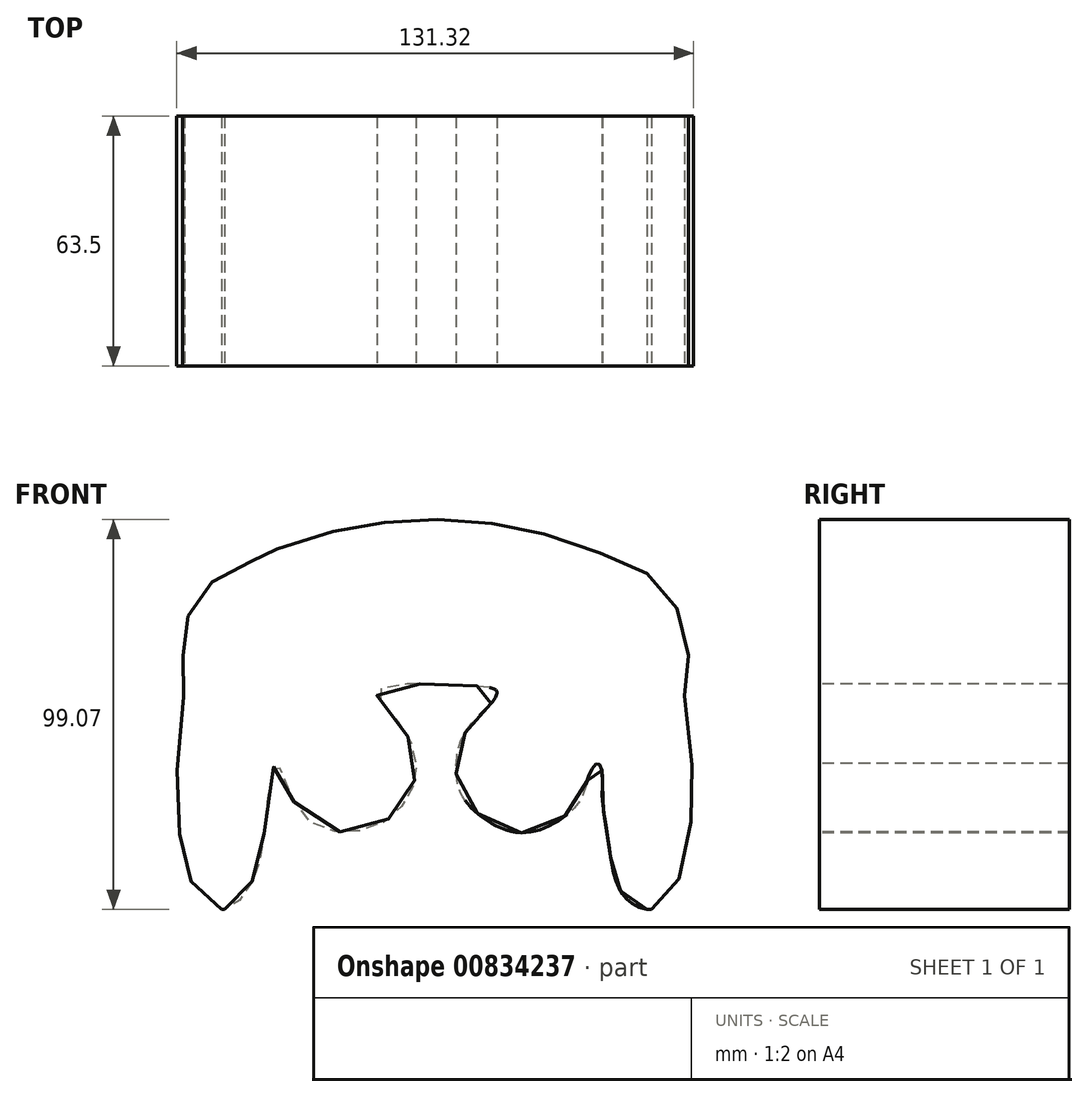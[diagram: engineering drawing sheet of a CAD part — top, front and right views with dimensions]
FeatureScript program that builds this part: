
annotation { "Feature Type Name" : "Feature", "Feature Type Description" : "" }
export const myFeature = defineFeature(function(context is Context, id is Id, definition is map)
    precondition{}
    {
        {
            var Q0;
            Q0=qCreatedBy(makeId("Front.planeOp"),FACE);
            var sketch = newSketch(context, id + "F0", { "sketchPlane" : qUnion([Q0])});
            skLineSegment(sketch, "E0.bottom", {"start": v(69.85, 50.8) * mm, "end": v(-69.85, 50.8) * mm});
            skLineSegment(sketch, "E0.top", {"start": v(69.85, -50.8) * mm, "end": v(-69.85, -50.8) * mm});
            skLineSegment(sketch, "E0.left", {"start": v(69.85, 50.8) * mm, "end": v(69.85, -50.8) * mm});
            skLineSegment(sketch, "E0.right", {"start": v(-69.85, 50.8) * mm, "end": v(-69.85, -50.8) * mm});
            skPoint(sketch, "E0.middle", {"position": v(0, 0) * mm});
            skSolve(sketch);
        }
        {
            var Q0;
            Q0=makeQuery(id+"F0.imprint","IMPRINT",FACE,{"disambiguationData":[TD([[makeQuery(id+"F0.imprint","IMPRINT",EDGE,{"derivedFrom":sQuery(id+"F0.wireOp",EDGE,"E0.bottom")}),1.0]])]});
            extrude(context, id + "F1", {"entities" : qUnion([Q0]), "depth" : 63.5 * mm, "offsetDistance" : 25.4 * mm});
        }
        {
            var Q0;
            Q0=makeQuery(id+"F1.opExtrude","CAP_FACE",FACE,{"disambiguationData":[OSD([sQuery(id+"F0.wireOp",EDGE,"E0.bottom"),sQuery(id+"F0.wireOp",EDGE,"E0.top"),sQuery(id+"F0.wireOp",EDGE,"E0.left"),sQuery(id+"F0.wireOp",EDGE,"E0.right")])],"isStart":false});
            var sketch = newSketch(context, id + "F2", { "sketchPlane" : qUnion([Q0])});
            skFitSpline(sketch, "E1", {"points": [v(0, 48.27) * mm, v(15.03, 47.3) * mm, v(29.07, 44.36) * mm, v(45.67, 38.5) * mm, v(56.3, 33.2) * mm, v(62.75, 23.96) * mm, v(64.87, 12.78) * mm, v(63.88, 5.12) * mm, v(66.07, -17.6) * mm, v(64.79, -32.74) * mm, v(60.06, -47.98) * mm, v(54.26, -50.8) * mm, v(49.52, -48.46) * mm, v(47.25, -45.36) * mm, v(45.47, -39.82) * mm, v(44.57, -33.56) * mm, v(42.96, -22.83) * mm, v(42.96, -16.21) * mm, v(41.89, -13.7) * mm, v(39.74, -16.27) * mm, v(37.49, -22.82) * mm, v(30.34, -29.13) * mm, v(21.4, -31.24) * mm, v(11.84, -26.94) * mm, v(6.48, -19.79) * mm, v(6.3, -10.3) * mm, v(8.8, -4.76) * mm, v(13.27, 0) * mm, v(16.18, 4.6) * mm, v(10.6, 5.97) * mm, v(-3.9, 6.5) * mm, v(-14.27, 4.36) * mm, v(-8.93, -3.18) * mm, v(-4.45, -12.75) * mm, v(-5.62, -20.77) * mm, v(-12.2, -28.36) * mm, v(-22.94, -31.13) * mm, v(-34.16, -25.5) * mm, v(-39.85, -13.7) * mm, v(-42.7, -28.55) * mm, v(-44.71, -40.67) * mm, v(-49.15, -48.4) * mm, v(-53.8, -50.8) * mm, v(-60.36, -45.63) * mm, v(-64, -34.81) * mm, v(-65.06, -16.03) * mm, v(-63.18, 8.09) * mm, v(-63.6, 13.93) * mm, v(-62.92, 22.06) * mm, v(-58.69, 29.58) * mm, v(-51.44, 35.66) * mm, v(-43.75, 38.48) * mm, v(-41.94, 39.69) * mm, v(-28.4, 44.5) * mm, v(-14.27, 47.36) * mm, v(0, 48.27) * mm]});
            skSolve(sketch);
        }
        {
            var Q0;
            {var subQ0=sQuery(id+"F2.wireOp",EDGE,"E1");var subQ1=makeQuery(id+"F1.opExtrude","CAP_EDGE",EDGE,{"disambiguationData":[OSD([sQuery(id+"F0.wireOp",EDGE,"E0.top")])],"isStart":false});var subQ2=makeQuery(id+"F2.imprint","INTERSECT",VERTEX,{"disambiguationData":[OD(0.0)],"derivedFrom":[subQ1,subQ0]});Q0=makeQuery(id+"F2.imprint","IMPRINT",FACE,{"disambiguationData":[TD([[makeQuery(id+"F2.imprint","IMPRINT",EDGE,{"disambiguationData":[TD([[subQ2,-1.0]])],"derivedFrom":subQ0}),1.0]])]});}
            var Q1;
            Q1=makeQuery(id+"F2.imprint","IMPRINT",FACE,{"disambiguationData":[TD([[makeQuery(id+"F2.imprint","IMPRINT",EDGE,{"derivedFrom":makeQuery(id+"F1.opExtrude","CAP_EDGE",EDGE,{"disambiguationData":[OSD([sQuery(id+"F0.wireOp",EDGE,"E0.bottom")])],"isStart":false})}),1.0]])]});
            extrude(context, id + "F3", {"entities" : qUnion([Q0, Q1]), "operationType" : NewBodyOperationType.REMOVE, "oppositeDirection" : true, "depth" : 63.5 * mm, "offsetDistance" : 25.4 * mm});
        }
    });
